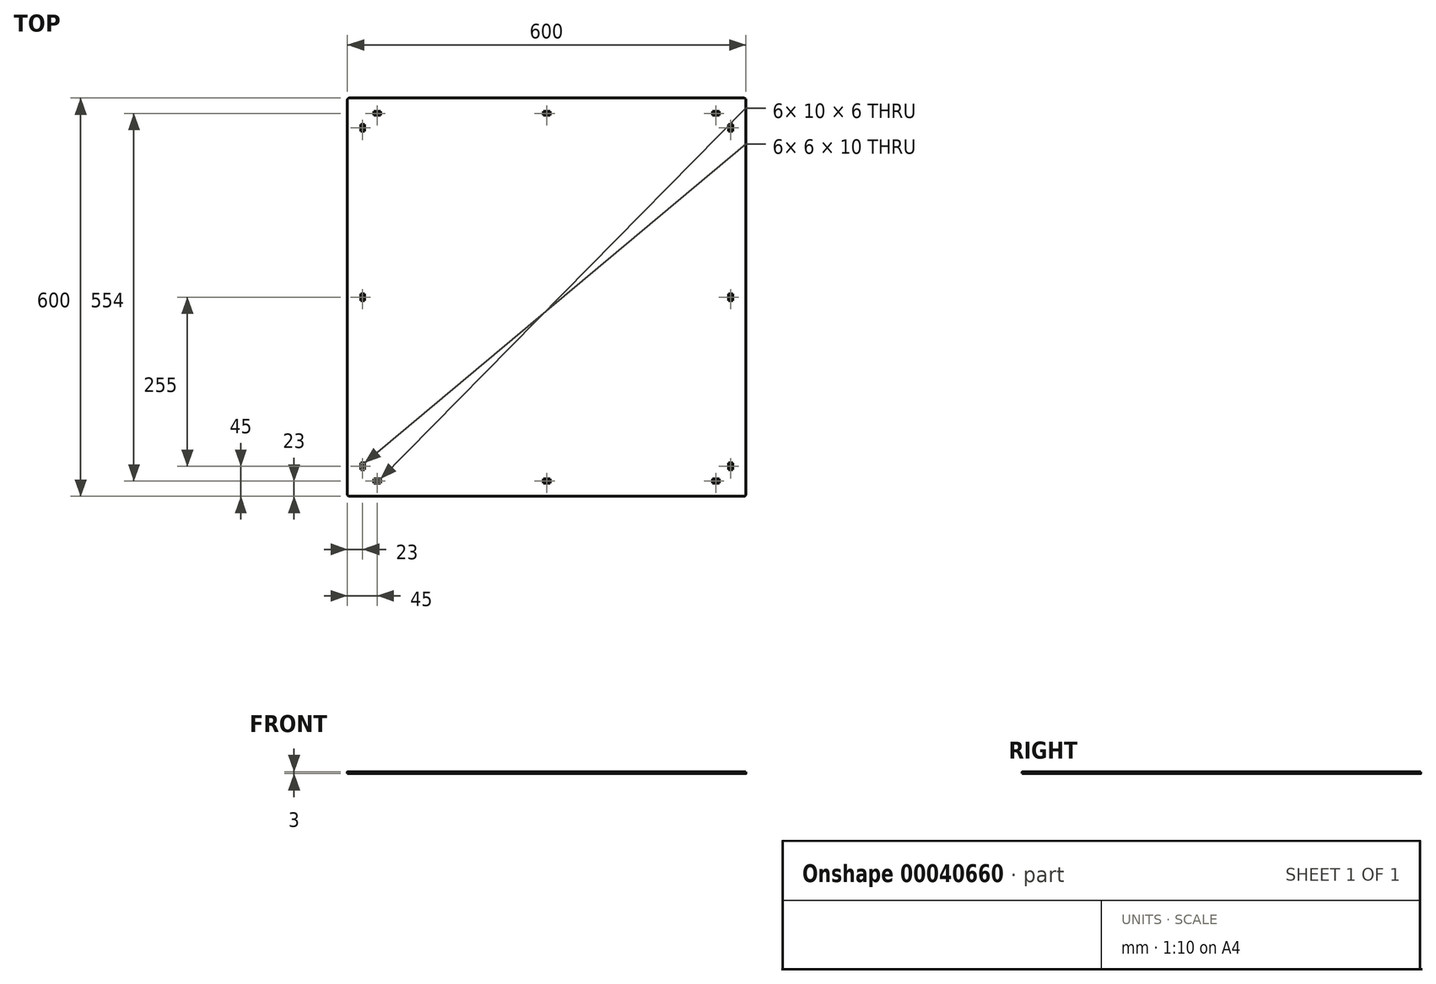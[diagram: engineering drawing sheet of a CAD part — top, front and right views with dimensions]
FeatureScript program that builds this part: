
annotation { "Feature Type Name" : "Feature", "Feature Type Description" : "" }
export const myFeature = defineFeature(function(context is Context, id is Id, definition is map)
    precondition{}
    {
        {
            var Q0;
            Q0=qCreatedBy(makeId("Top.planeOp"),FACE);
            var sketch = newSketch(context, id + "F0", { "sketchPlane" : qUnion([Q0])});
            skLineSegment(sketch, "E0.bottom", {"start": v(300, -300) * mm, "end": v(-300, -300) * mm});
            skLineSegment(sketch, "E0.top", {"start": v(300, 300) * mm, "end": v(-300, 300) * mm});
            skLineSegment(sketch, "E0.left", {"start": v(300, -300) * mm, "end": v(300, 300) * mm});
            skLineSegment(sketch, "E0.right", {"start": v(-300, -300) * mm, "end": v(-300, 300) * mm});
            skPoint(sketch, "E0.middle", {"position": v(0, 0) * mm});
            skLineSegment(sketch, "E1.bottom", {"start": v(-260, 280) * mm, "end": v(-250, 280) * mm});
            skLineSegment(sketch, "E1.top", {"start": v(-260, 274) * mm, "end": v(-250, 274) * mm});
            skLineSegment(sketch, "E1.left", {"start": v(-260, 280) * mm, "end": v(-260, 274) * mm});
            skLineSegment(sketch, "E1.right", {"start": v(-250, 280) * mm, "end": v(-250, 274) * mm});
            skLineSegment(sketch, "E2.MirrorCS", {"start": v(260, 280) * mm, "end": v(250, 280) * mm});
            skLineSegment(sketch, "E3.MirrorCS", {"start": v(250, 280) * mm, "end": v(250, 274) * mm});
            skLineSegment(sketch, "E4.MirrorCS", {"start": v(260, 274) * mm, "end": v(250, 274) * mm});
            skLineSegment(sketch, "E5.MirrorCS", {"start": v(260, 280) * mm, "end": v(260, 274) * mm});
            skLineSegment(sketch, "E6.MirrorCS", {"start": v(-260, -280) * mm, "end": v(-260, -274) * mm});
            skLineSegment(sketch, "E7.MirrorCS", {"start": v(-260, -280) * mm, "end": v(-250, -280) * mm});
            skLineSegment(sketch, "E8.MirrorCS", {"start": v(-260, -274) * mm, "end": v(-250, -274) * mm});
            skLineSegment(sketch, "E9.MirrorCS", {"start": v(-250, -280) * mm, "end": v(-250, -274) * mm});
            skLineSegment(sketch, "E10.MirrorCS", {"start": v(250, -280) * mm, "end": v(250, -274) * mm});
            skLineSegment(sketch, "E11.MirrorCS", {"start": v(260, -280) * mm, "end": v(250, -280) * mm});
            skLineSegment(sketch, "E12.MirrorCS", {"start": v(260, -274) * mm, "end": v(250, -274) * mm});
            skLineSegment(sketch, "E13.MirrorCS", {"start": v(260, -280) * mm, "end": v(260, -274) * mm});
            skLineSegment(sketch, "E14.bottom", {"start": v(-280, 260) * mm, "end": v(-274, 260) * mm});
            skLineSegment(sketch, "E14.top", {"start": v(-280, 250) * mm, "end": v(-274, 250) * mm});
            skLineSegment(sketch, "E14.left", {"start": v(-280, 260) * mm, "end": v(-280, 250) * mm});
            skLineSegment(sketch, "E14.right", {"start": v(-274, 260) * mm, "end": v(-274, 250) * mm});
            skLineSegment(sketch, "E15.MirrorCS", {"start": v(280, 250) * mm, "end": v(274, 250) * mm});
            skLineSegment(sketch, "E16.MirrorCS", {"start": v(274, 260) * mm, "end": v(274, 250) * mm});
            skLineSegment(sketch, "E17.MirrorCS", {"start": v(280, 260) * mm, "end": v(274, 260) * mm});
            skLineSegment(sketch, "E18.MirrorCS", {"start": v(280, 260) * mm, "end": v(280, 250) * mm});
            skLineSegment(sketch, "E19.MirrorCS", {"start": v(280, -260) * mm, "end": v(274, -260) * mm});
            skLineSegment(sketch, "E20.MirrorCS", {"start": v(274, -260) * mm, "end": v(274, -250) * mm});
            skLineSegment(sketch, "E21.MirrorCS", {"start": v(280, -250) * mm, "end": v(274, -250) * mm});
            skLineSegment(sketch, "E22.MirrorCS", {"start": v(280, -260) * mm, "end": v(280, -250) * mm});
            skLineSegment(sketch, "E23.MirrorCS", {"start": v(-280, -260) * mm, "end": v(-280, -250) * mm});
            skLineSegment(sketch, "E24.MirrorCS", {"start": v(-280, -260) * mm, "end": v(-274, -260) * mm});
            skLineSegment(sketch, "E25.MirrorCS", {"start": v(-274, -260) * mm, "end": v(-274, -250) * mm});
            skLineSegment(sketch, "E26.MirrorCS", {"start": v(-280, -250) * mm, "end": v(-274, -250) * mm});
            skLineSegment(sketch, "E27.bottom", {"start": v(5, 274) * mm, "end": v(-5, 274) * mm});
            skLineSegment(sketch, "E27.top", {"start": v(5, 280) * mm, "end": v(-5, 280) * mm});
            skLineSegment(sketch, "E27.left", {"start": v(5, 274) * mm, "end": v(5, 280) * mm});
            skLineSegment(sketch, "E27.right", {"start": v(-5, 274) * mm, "end": v(-5, 280) * mm});
            skPoint(sketch, "E27.middle", {"position": v(0, 277) * mm});
            skLineSegment(sketch, "E28.bottom", {"start": v(-274, -5) * mm, "end": v(-280, -5) * mm});
            skLineSegment(sketch, "E28.top", {"start": v(-274, 5) * mm, "end": v(-280, 5) * mm});
            skLineSegment(sketch, "E28.left", {"start": v(-274, -5) * mm, "end": v(-274, 5) * mm});
            skLineSegment(sketch, "E28.right", {"start": v(-280, -5) * mm, "end": v(-280, 5) * mm});
            skPoint(sketch, "E28.middle", {"position": v(-277, 0) * mm});
            skLineSegment(sketch, "E29.MirrorCS", {"start": v(-5, -274) * mm, "end": v(-5, -280) * mm});
            skLineSegment(sketch, "E30.MirrorCS", {"start": v(5, -280) * mm, "end": v(-5, -280) * mm});
            skLineSegment(sketch, "E31.MirrorCS", {"start": v(5, -274) * mm, "end": v(-5, -274) * mm});
            skLineSegment(sketch, "E32.MirrorCS", {"start": v(5, -274) * mm, "end": v(5, -280) * mm});
            skLineSegment(sketch, "E33.MirrorCS", {"start": v(274, -5) * mm, "end": v(280, -5) * mm});
            skLineSegment(sketch, "E34.MirrorCS", {"start": v(274, -5) * mm, "end": v(274, 5) * mm});
            skLineSegment(sketch, "E35.MirrorCS", {"start": v(280, -5) * mm, "end": v(280, 5) * mm});
            skLineSegment(sketch, "E36.MirrorCS", {"start": v(274, 5) * mm, "end": v(280, 5) * mm});
            skSolve(sketch);
        }
        {
            var Q0;
            Q0=makeQuery(id+"F0.imprint","IMPRINT",FACE,{"disambiguationData":[TD([[makeQuery(id+"F0.imprint","IMPRINT",EDGE,{"derivedFrom":sQuery(id+"F0.wireOp",EDGE,"E0.bottom")}),-1.0]])]});
            extrude(context, id + "F1", {"entities" : qUnion([Q0]), "depth" : 3 * mm});
        }
        {
            var Q0;
            Q0=makeQuery(id+"F1.opExtrude","SWEPT_EDGE",EDGE,{"disambiguationData":[OSD([sQuery(id+"F0.wireOp",EDGE,"E0.top"),sQuery(id+"F0.wireOp",EDGE,"E0.left")])]});
            var Q1;
            Q1=makeQuery(id+"F1.opExtrude","SWEPT_EDGE",EDGE,{"disambiguationData":[OSD([sQuery(id+"F0.wireOp",EDGE,"E0.bottom"),sQuery(id+"F0.wireOp",EDGE,"E0.left")])]});
            var Q2;
            Q2=makeQuery(id+"F1.opExtrude","SWEPT_EDGE",EDGE,{"disambiguationData":[OSD([sQuery(id+"F0.wireOp",EDGE,"E0.bottom"),sQuery(id+"F0.wireOp",EDGE,"E0.right")])]});
            var Q3;
            Q3=makeQuery(id+"F1.opExtrude","SWEPT_EDGE",EDGE,{"disambiguationData":[OSD([sQuery(id+"F0.wireOp",EDGE,"E0.top"),sQuery(id+"F0.wireOp",EDGE,"E0.right")])]});
            fillet(context, id + "F2", {"entities" : qUnion([Q0, Q1, Q2, Q3]), "radius" : 3 * mm, "tangentPropagation" : true, "allowEdgeOverflow" : false});
        }
    });
